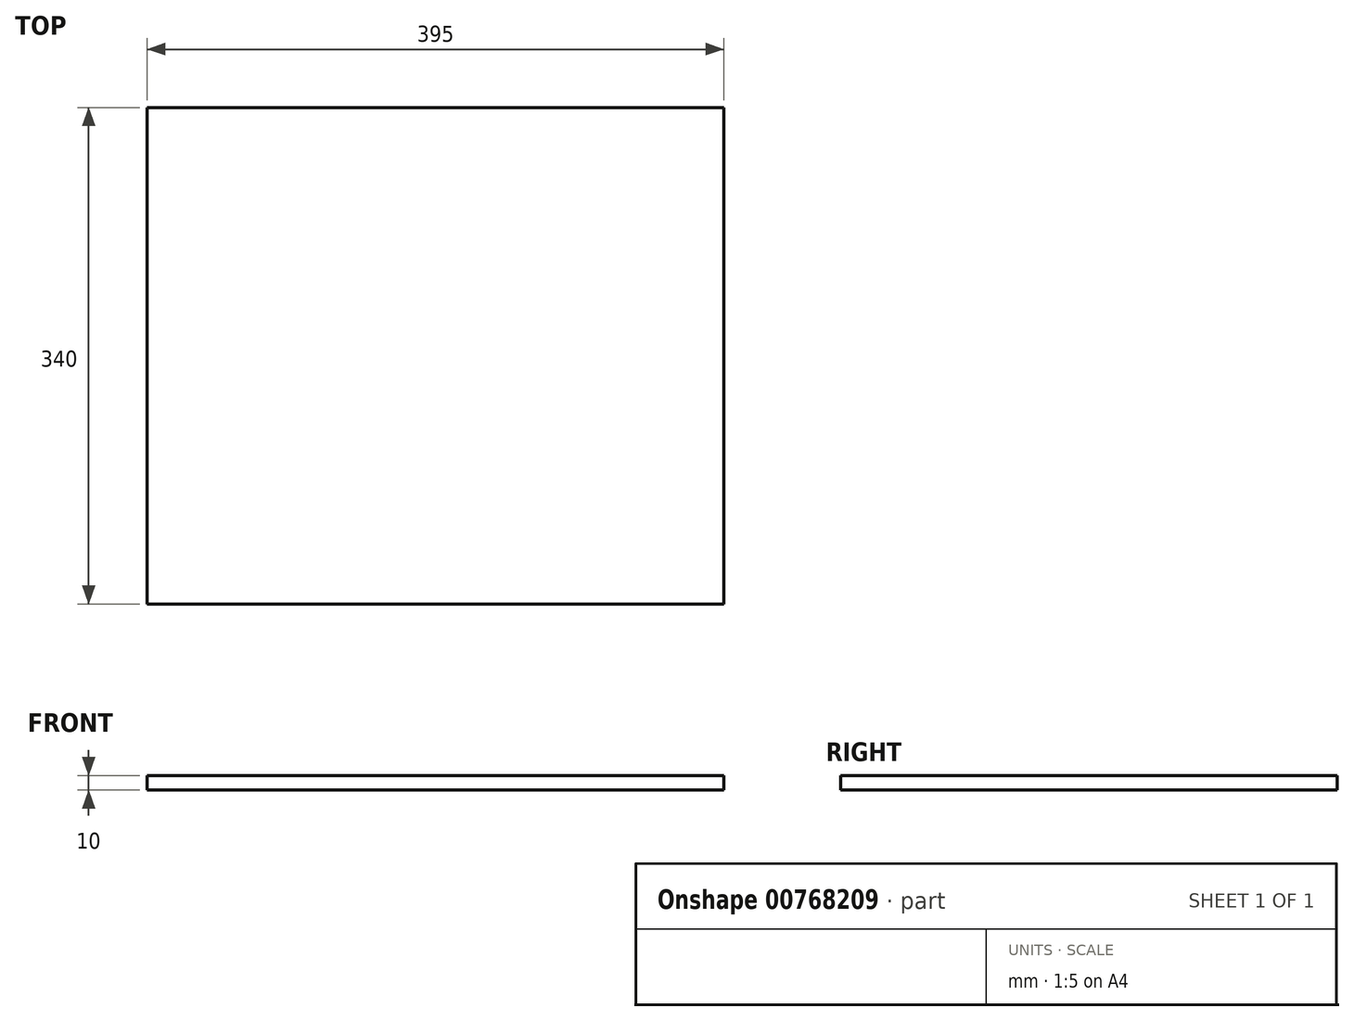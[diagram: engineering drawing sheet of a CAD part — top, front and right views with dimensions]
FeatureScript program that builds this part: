
annotation { "Feature Type Name" : "Feature", "Feature Type Description" : "" }
export const myFeature = defineFeature(function(context is Context, id is Id, definition is map)
    precondition{}
    {
        {
            var Q0;
            Q0=qCreatedBy(makeId("Top.planeOp"),FACE);
            var sketch = newSketch(context, id + "F0", { "sketchPlane" : qUnion([Q0])});
            skLineSegment(sketch, "E0.bottom", {"start": v(-70.96, 65.05) * mm, "end": v(324.04, 65.05) * mm});
            skLineSegment(sketch, "E0.top", {"start": v(-70.96, -274.95) * mm, "end": v(324.04, -274.95) * mm});
            skLineSegment(sketch, "E0.left", {"start": v(-70.96, 65.05) * mm, "end": v(-70.96, -274.95) * mm});
            skLineSegment(sketch, "E0.right", {"start": v(324.04, 65.05) * mm, "end": v(324.04, -274.95) * mm});
            skSolve(sketch);
        }
        {
            var Q0;
            Q0=qSketchRegion(id+"F0",true);
            extrude(context, id + "F1", {"entities" : qUnion([Q0]), "depth" : 10 * mm});
        }
    });
